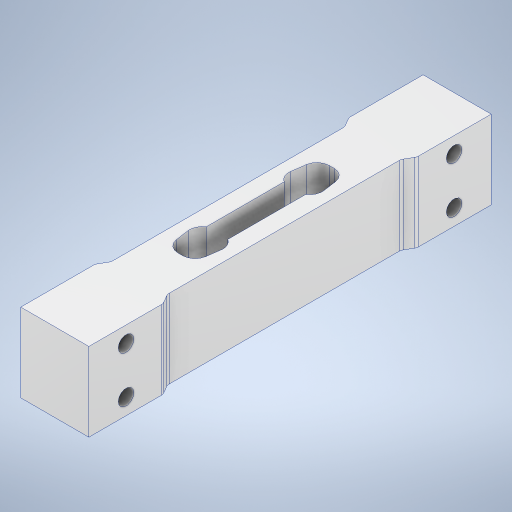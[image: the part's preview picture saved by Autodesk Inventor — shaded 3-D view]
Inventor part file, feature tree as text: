
AUTODESK INVENTOR PART (.ipt)
format: ipt  version: 2023.2 (Build 272271030, 271C)  size: 343,552 bytes
history: native  units: mm
features: sketch x2, other x1, extrude x1, hole x1
ambient origin geometry x8: Origin, YZ Plane, XZ Plane, XY Plane, X Axis, Y Axis, Z Axis, Center Point
bodies: Body1 (feature_tree)
feature tree (5):
  other  "Sólido1"
  extrude  "Extrusão1"  Depth=22.0mm
  hole  "Furo1"  [1 undecoded]
  sketch  "Esboço1"  dims[d0=22.0mm d1=24.0mm]
  sketch  "Esboço2"  dims[d4=3.8mm d6=3.8mm d7=24.0mm d8=18.2mm d10=0.0mm d11=130.0mm d12=1.9mm d13=2.0mm d14=2.0mm d38=7.0mm d39=7.0mm d40=4.495648mm d41=4.495648mm d42=4.451897mm d43=0.625673mm d44=30.019663mm d45=1.545706mm d46=1.545706mm d47=0.625673mm d48=4.451897mm d49=3.961072mm d50=3.443308mm d51=9.467851mm d52=3.961072mm d53=3.960192mm d54=1.859599mm d55=4.451897mm d56=3.960192mm d57=3.960192mm d58=4.375069mm d59=1.859599mm d60=3.961072mm d61=3.961072mm d62=3.443308mm d63=3.443308mm d64=0.0mm d65=48.903794mm d67=0.0mm d68=25.4mm d69=0.0mm d70=15.0mm d72=25.4mm d73=5.2mm d74=0.0mm d75=12.0mm d76=15.0mm d77=12.0mm d78=0.0mm d79=5.2mm d80=5.0mm d81=6.0mm d82=3.023mm d83=2.0mm d84=14.3117mm d85=0.5mm d86=20.594885mm]
note: 1 required parameter value undecoded (feature->parameter linkage not recoverable at this tier; creation-order binding heuristic only, values carry confidence <= 0.55)
